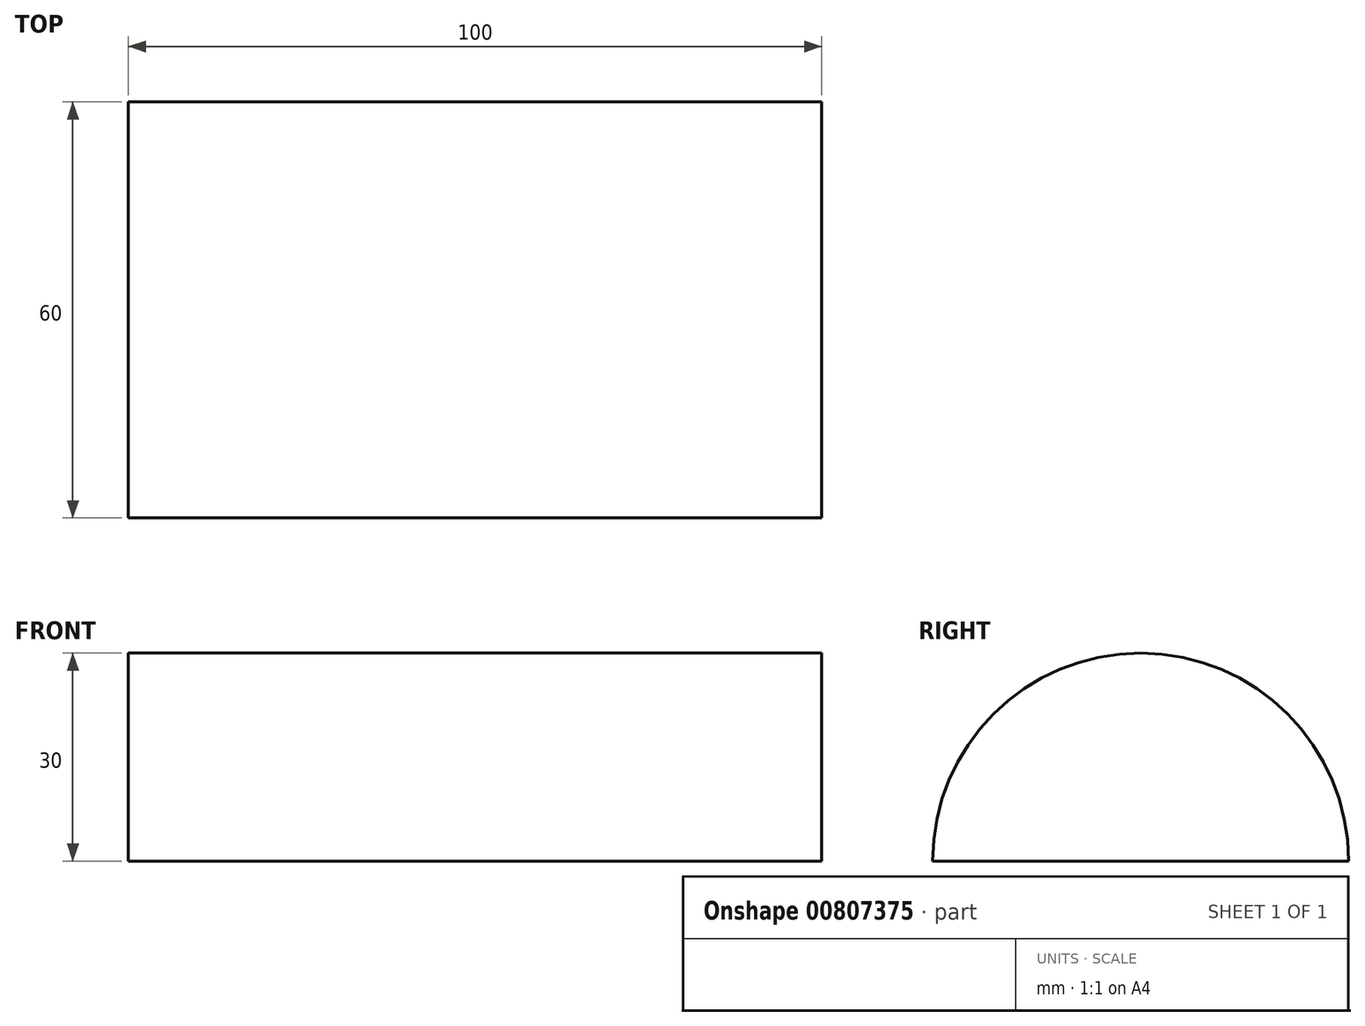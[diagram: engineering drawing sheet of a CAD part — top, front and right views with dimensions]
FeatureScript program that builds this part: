
annotation { "Feature Type Name" : "Feature", "Feature Type Description" : "" }
export const myFeature = defineFeature(function(context is Context, id is Id, definition is map)
    precondition{}
    {
        {
            var Q0;
            Q0=qCreatedBy(makeId("Front.planeOp"),FACE);
            var sketch = newSketch(context, id + "F0", { "sketchPlane" : qUnion([Q0])});
            skLineSegment(sketch, "E0.bottom", {"start": v(-51.95, 0) * mm, "end": v(48.05, 0) * mm});
            skLineSegment(sketch, "E0.top", {"start": v(-51.95, 30) * mm, "end": v(48.05, 30) * mm});
            skLineSegment(sketch, "E0.left", {"start": v(-51.95, 0) * mm, "end": v(-51.95, 30) * mm});
            skLineSegment(sketch, "E0.right", {"start": v(48.05, 0) * mm, "end": v(48.05, 30) * mm});
            skLineSegment(sketch, "E1", {"start": v(-51.95, 0) * mm, "end": v(-73.7, 0) * mm, "construction": true});
            skLineSegment(sketch, "E2", {"start": v(48.05, 0) * mm, "end": v(73.7, 0) * mm, "construction": true});
            skSolve(sketch);
        }
        {
            var Q0;
            Q0=makeQuery(id+"F0.imprint","IMPRINT",FACE,{"disambiguationData":[TD([[makeQuery(id+"F0.imprint","IMPRINT",EDGE,{"derivedFrom":sQuery(id+"F0.wireOp",EDGE,"E0.bottom")}),1.0]])]});
            var Q1;
            Q1=sQuery(id+"F0.wireOp",EDGE,"E0.bottom");
            revolve(context, id + "F1", {"surfaceOperationType" : NewSurfaceOperationType.NEW, "entities" : qUnion([Q0]), "axis" : qUnion([Q1]), "revolveType" : RevolveType.SYMMETRIC, "oppositeDirection" : true, "angle" : 180 * degree});
        }
    });
